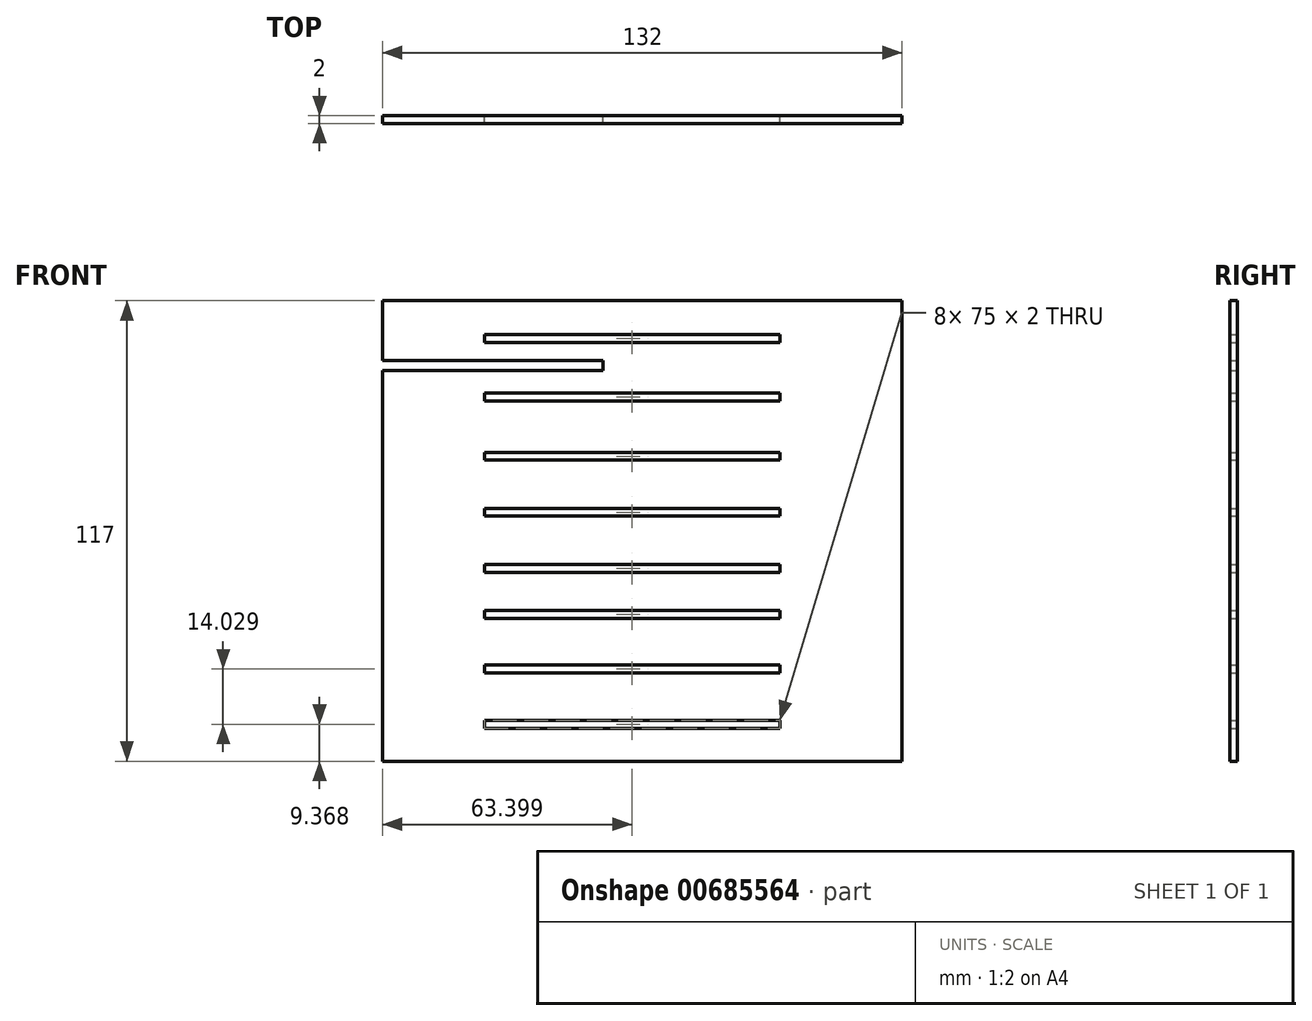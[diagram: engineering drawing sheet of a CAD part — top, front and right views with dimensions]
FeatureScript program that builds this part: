
annotation { "Feature Type Name" : "Feature", "Feature Type Description" : "" }
export const myFeature = defineFeature(function(context is Context, id is Id, definition is map)
    precondition{}
    {
        {
            var Q0;
            Q0=qCreatedBy(makeId("Front.planeOp"),FACE);
            var sketch = newSketch(context, id + "F0", { "sketchPlane" : qUnion([Q0])});
            skLineSegment(sketch, "E0.bottom", {"start": v(-36.75, -57.98) * mm, "end": v(38.25, -57.98) * mm});
            skLineSegment(sketch, "E0.top", {"start": v(-36.75, -59.98) * mm, "end": v(38.25, -59.98) * mm});
            skLineSegment(sketch, "E0.left", {"start": v(-36.75, -57.98) * mm, "end": v(-36.75, -59.98) * mm});
            skLineSegment(sketch, "E0.right", {"start": v(38.25, -57.98) * mm, "end": v(38.25, -59.98) * mm});
            skLineSegment(sketch, "E1.bottom", {"start": v(-53.7, -51.72) * mm, "end": v(-6.7, -51.72) * mm});
            skLineSegment(sketch, "E1.top", {"start": v(-53.7, -54.22) * mm, "end": v(-6.7, -54.22) * mm});
            skLineSegment(sketch, "E1.right", {"start": v(-6.7, -51.72) * mm, "end": v(-6.7, -54.22) * mm});
            skLineSegment(sketch, "E2.bottom", {"start": v(56.3, -51.72) * mm, "end": v(9.3, -51.72) * mm});
            skLineSegment(sketch, "E2.top", {"start": v(56.3, -54.22) * mm, "end": v(9.3, -54.22) * mm});
            skLineSegment(sketch, "E2.right", {"start": v(9.3, -51.72) * mm, "end": v(9.3, -54.22) * mm});
            skLineSegment(sketch, "E3.bottom", {"start": v(-36.75, -43.95) * mm, "end": v(38.25, -43.95) * mm});
            skLineSegment(sketch, "E3.top", {"start": v(-36.75, -45.95) * mm, "end": v(38.25, -45.95) * mm});
            skLineSegment(sketch, "E3.left", {"start": v(-36.75, -43.95) * mm, "end": v(-36.75, -45.95) * mm});
            skLineSegment(sketch, "E3.right", {"start": v(38.25, -43.95) * mm, "end": v(38.25, -45.95) * mm});
            skLineSegment(sketch, "E4.bottom", {"start": v(-53.7, -37.44) * mm, "end": v(-6.7, -37.44) * mm});
            skLineSegment(sketch, "E4.top", {"start": v(-53.7, -39.94) * mm, "end": v(-6.7, -39.94) * mm});
            skLineSegment(sketch, "E4.right", {"start": v(-6.7, -37.44) * mm, "end": v(-6.7, -39.94) * mm});
            skLineSegment(sketch, "E5.bottom", {"start": v(56.3, -37.44) * mm, "end": v(9.3, -37.44) * mm});
            skLineSegment(sketch, "E5.top", {"start": v(56.3, -39.94) * mm, "end": v(9.3, -39.94) * mm});
            skLineSegment(sketch, "E5.right", {"start": v(9.3, -37.44) * mm, "end": v(9.3, -39.94) * mm});
            skLineSegment(sketch, "E6.bottom", {"start": v(-36.75, -30.05) * mm, "end": v(38.25, -30.05) * mm});
            skLineSegment(sketch, "E6.top", {"start": v(-36.75, -32.05) * mm, "end": v(38.25, -32.05) * mm});
            skLineSegment(sketch, "E6.left", {"start": v(-36.75, -30.05) * mm, "end": v(-36.75, -32.05) * mm});
            skLineSegment(sketch, "E6.right", {"start": v(38.25, -30.05) * mm, "end": v(38.25, -32.05) * mm});
            skLineSegment(sketch, "E7.bottom", {"start": v(-53.7, -23.9) * mm, "end": v(-6.7, -23.9) * mm});
            skLineSegment(sketch, "E7.top", {"start": v(-53.7, -26.4) * mm, "end": v(-6.7, -26.4) * mm});
            skLineSegment(sketch, "E7.right", {"start": v(-6.7, -23.9) * mm, "end": v(-6.7, -26.4) * mm});
            skLineSegment(sketch, "E8.bottom", {"start": v(56.3, -23.9) * mm, "end": v(9.3, -23.9) * mm});
            skLineSegment(sketch, "E8.top", {"start": v(56.3, -26.4) * mm, "end": v(9.3, -26.4) * mm});
            skLineSegment(sketch, "E8.right", {"start": v(9.3, -23.9) * mm, "end": v(9.3, -26.4) * mm});
            skLineSegment(sketch, "E9.bottom", {"start": v(-36.75, -18.4) * mm, "end": v(38.25, -18.4) * mm});
            skLineSegment(sketch, "E9.top", {"start": v(-36.75, -20.4) * mm, "end": v(38.25, -20.4) * mm});
            skLineSegment(sketch, "E9.left", {"start": v(-36.75, -18.4) * mm, "end": v(-36.75, -20.4) * mm});
            skLineSegment(sketch, "E9.right", {"start": v(38.25, -18.4) * mm, "end": v(38.25, -20.4) * mm});
            skLineSegment(sketch, "E10.bottom", {"start": v(-53.7, -10.37) * mm, "end": v(-6.7, -10.37) * mm});
            skLineSegment(sketch, "E10.top", {"start": v(-53.7, -12.87) * mm, "end": v(-6.7, -12.87) * mm});
            skLineSegment(sketch, "E10.right", {"start": v(-6.7, -10.37) * mm, "end": v(-6.7, -12.87) * mm});
            skLineSegment(sketch, "E11.bottom", {"start": v(56.3, -10.37) * mm, "end": v(9.3, -10.37) * mm});
            skLineSegment(sketch, "E11.top", {"start": v(56.3, -12.87) * mm, "end": v(9.3, -12.87) * mm});
            skLineSegment(sketch, "E11.right", {"start": v(9.3, -10.37) * mm, "end": v(9.3, -12.87) * mm});
            skLineSegment(sketch, "E12.bottom", {"start": v(-36.75, -4.1) * mm, "end": v(38.25, -4.1) * mm});
            skLineSegment(sketch, "E12.top", {"start": v(-36.75, -6.1) * mm, "end": v(38.25, -6.1) * mm});
            skLineSegment(sketch, "E12.left", {"start": v(-36.75, -4.1) * mm, "end": v(-36.75, -6.1) * mm});
            skLineSegment(sketch, "E12.right", {"start": v(38.25, -4.1) * mm, "end": v(38.25, -6.1) * mm});
            skLineSegment(sketch, "E13.bottom", {"start": v(-53.7, 2.5) * mm, "end": v(-6.7, 2.5) * mm});
            skLineSegment(sketch, "E13.top", {"start": v(-53.7, 0) * mm, "end": v(-6.7, 0) * mm});
            skLineSegment(sketch, "E13.right", {"start": v(-6.7, 2.5) * mm, "end": v(-6.7, 0) * mm});
            skLineSegment(sketch, "E14.bottom", {"start": v(56.3, 2.5) * mm, "end": v(9.3, 2.5) * mm});
            skLineSegment(sketch, "E14.top", {"start": v(56.3, 0) * mm, "end": v(9.3, 0) * mm});
            skLineSegment(sketch, "E14.right", {"start": v(9.3, 2.5) * mm, "end": v(9.3, 0) * mm});
            skPoint(sketch, "E15.firstSnap0", {"position": v(-14.77, 8.13) * mm});
            skLineSegment(sketch, "E15.bottom", {"start": v(-36.75, 8.13) * mm, "end": v(38.25, 8.13) * mm});
            skLineSegment(sketch, "E15.top", {"start": v(-36.75, 10.13) * mm, "end": v(38.25, 10.13) * mm});
            skLineSegment(sketch, "E15.left", {"start": v(-36.75, 8.13) * mm, "end": v(-36.75, 10.13) * mm});
            skLineSegment(sketch, "E15.right", {"start": v(38.25, 8.13) * mm, "end": v(38.25, 10.13) * mm});
            skLineSegment(sketch, "E16.bottom", {"start": v(-53.7, 18) * mm, "end": v(-6.7, 18) * mm});
            skLineSegment(sketch, "E16.top", {"start": v(-53.7, 15.5) * mm, "end": v(-6.7, 15.5) * mm});
            skLineSegment(sketch, "E16.right", {"start": v(-6.7, 18) * mm, "end": v(-6.7, 15.5) * mm});
            skLineSegment(sketch, "E17.bottom", {"start": v(56.3, 18) * mm, "end": v(9.3, 18) * mm});
            skLineSegment(sketch, "E17.top", {"start": v(56.3, 15.5) * mm, "end": v(9.3, 15.5) * mm});
            skLineSegment(sketch, "E17.right", {"start": v(9.3, 18) * mm, "end": v(9.3, 15.5) * mm});
            skLineSegment(sketch, "E18.bottom", {"start": v(-36.75, 25.21) * mm, "end": v(38.25, 25.21) * mm});
            skLineSegment(sketch, "E18.top", {"start": v(-36.75, 23.21) * mm, "end": v(38.25, 23.21) * mm});
            skLineSegment(sketch, "E18.left", {"start": v(-36.75, 25.21) * mm, "end": v(-36.75, 23.21) * mm});
            skLineSegment(sketch, "E18.right", {"start": v(38.25, 25.21) * mm, "end": v(38.25, 23.21) * mm});
            skLineSegment(sketch, "E19.bottom", {"start": v(-53.7, 33.42) * mm, "end": v(-6.7, 33.42) * mm});
            skLineSegment(sketch, "E19.top", {"start": v(-53.7, 30.92) * mm, "end": v(-6.7, 30.92) * mm});
            skLineSegment(sketch, "E19.right", {"start": v(-6.7, 33.42) * mm, "end": v(-6.7, 30.92) * mm});
            skLineSegment(sketch, "E20.bottom", {"start": v(56.3, 33.42) * mm, "end": v(9.3, 33.42) * mm});
            skLineSegment(sketch, "E20.top", {"start": v(56.3, 30.92) * mm, "end": v(9.3, 30.92) * mm});
            skLineSegment(sketch, "E20.right", {"start": v(9.3, 33.42) * mm, "end": v(9.3, 30.92) * mm});
            skLineSegment(sketch, "E21.bottom", {"start": v(-36.75, 40.06) * mm, "end": v(38.25, 40.06) * mm});
            skLineSegment(sketch, "E21.top", {"start": v(-36.75, 38.06) * mm, "end": v(38.25, 38.06) * mm});
            skLineSegment(sketch, "E21.left", {"start": v(-36.75, 40.06) * mm, "end": v(-36.75, 38.06) * mm});
            skLineSegment(sketch, "E21.right", {"start": v(38.25, 40.06) * mm, "end": v(38.25, 38.06) * mm});
            skPoint(sketch, "E22.bottom.start.orphan", {"position": v(24.15, 53.7) * mm});
            skLineSegment(sketch, "E23", {"start": v(56.3, -62.69) * mm, "end": v(-53.7, -62.69) * mm});
            skLineSegment(sketch, "E24", {"start": v(-53.7, -62.69) * mm, "end": v(-53.7, -54.22) * mm});
            skLineSegment(sketch, "E25.trimOffspring", {"start": v(-53.7, 18) * mm, "end": v(-53.7, 30.92) * mm});
            skLineSegment(sketch, "E26.trimOffspring", {"start": v(-53.7, 33.42) * mm, "end": v(-53.7, 43.9) * mm});
            skLineSegment(sketch, "E27.trimOffspring", {"start": v(-53.7, -23.9) * mm, "end": v(-53.7, -12.87) * mm});
            skLineSegment(sketch, "E28.trimOffspring", {"start": v(-53.7, -37.44) * mm, "end": v(-53.7, -26.4) * mm});
            skLineSegment(sketch, "E29.trimOffspring", {"start": v(-53.7, -51.72) * mm, "end": v(-53.7, -39.94) * mm});
            skLineSegment(sketch, "E30", {"start": v(-53.7, 15.5) * mm, "end": v(-53.7, 2.5) * mm});
            skLineSegment(sketch, "E31", {"start": v(-53.7, 0) * mm, "end": v(-53.7, -10.37) * mm});
            skPoint(sketch, "E32.end.orphan", {"position": v(56.3, 38.06) * mm});
            skLineSegment(sketch, "E33", {"start": v(56.3, 30.92) * mm, "end": v(56.3, 18) * mm});
            skLineSegment(sketch, "E34", {"start": v(56.3, 15.5) * mm, "end": v(56.3, 2.5) * mm});
            skLineSegment(sketch, "E35", {"start": v(56.3, 0) * mm, "end": v(56.3, -10.37) * mm});
            skLineSegment(sketch, "E36", {"start": v(56.3, -12.87) * mm, "end": v(56.3, -23.9) * mm});
            skLineSegment(sketch, "E37", {"start": v(56.3, -26.4) * mm, "end": v(56.3, -37.44) * mm});
            skLineSegment(sketch, "E38", {"start": v(56.3, -39.94) * mm, "end": v(56.3, -51.72) * mm});
            skLineSegment(sketch, "E39", {"start": v(56.3, -55.54) * mm, "end": v(56.3, -62.69) * mm});
            skPoint(sketch, "E40.end.orphan", {"position": v(55.92, 33.42) * mm});
            skLineSegment(sketch, "E41", {"start": v(-53.7, 43.9) * mm, "end": v(53.85, 43.9) * mm});
            skLineSegment(sketch, "E42", {"start": v(56.3, 33.42) * mm, "end": v(56.3, 43.93) * mm});
            skLineSegment(sketch, "E43", {"start": v(56.3, 43.93) * mm, "end": v(53.85, 43.9) * mm});
            skLineSegment(sketch, "E44.bottom", {"start": v(-62.65, 48.65) * mm, "end": v(69.35, 48.65) * mm});
            skLineSegment(sketch, "E44.top", {"start": v(-62.65, -68.35) * mm, "end": v(69.35, -68.35) * mm});
            skLineSegment(sketch, "E44.left", {"start": v(-62.65, 48.65) * mm, "end": v(-62.65, 33.42) * mm});
            skLineSegment(sketch, "E44.right", {"start": v(69.35, 48.65) * mm, "end": v(69.35, -68.35) * mm});
            skLineSegment(sketch, "E45", {"start": v(-53.7, 33.42) * mm, "end": v(-62.65, 33.42) * mm});
            skLineSegment(sketch, "E46", {"start": v(-53.7, 30.92) * mm, "end": v(-62.65, 30.92) * mm});
            skLineSegment(sketch, "E47.trimOffspring", {"start": v(-62.65, 30.92) * mm, "end": v(-62.65, -68.35) * mm});
            skLineSegment(sketch, "E48", {"start": v(-53.7, 18) * mm, "end": v(-62.65, 18) * mm});
            skLineSegment(sketch, "E49", {"start": v(-62.65, 18) * mm, "end": v(-62.65, 15.5) * mm});
            skLineSegment(sketch, "E50", {"start": v(-62.65, 15.5) * mm, "end": v(-53.7, 15.5) * mm});
            skLineSegment(sketch, "E51", {"start": v(-53.7, 2.5) * mm, "end": v(-62.65, 2.5) * mm});
            skLineSegment(sketch, "E52", {"start": v(-62.65, 2.5) * mm, "end": v(-62.65, 0) * mm});
            skLineSegment(sketch, "E53", {"start": v(-62.65, 0) * mm, "end": v(-53.7, 0) * mm});
            skLineSegment(sketch, "E54", {"start": v(-53.7, -10.37) * mm, "end": v(-62.65, -10.37) * mm});
            skLineSegment(sketch, "E55", {"start": v(-62.65, -10.37) * mm, "end": v(-62.65, -12.87) * mm});
            skLineSegment(sketch, "E56", {"start": v(-62.65, -12.87) * mm, "end": v(-53.7, -12.87) * mm});
            skSolve(sketch);
        }
        {
            var Q0;
            Q0 = qSketchRegion(id + "F0", true);
            extrude(context, id + "F1", {"entities" : qUnion([Q0]), "depth" : 1 * mm, "offsetDistance" : 25 * mm});
        }
        {
            var Q0;
            Q0 = qSketchRegion(id + "F0", true);
            extrude(context, id + "F2", {"entities" : qUnion([Q0]), "operationType" : NewBodyOperationType.ADD, "depth" : 2 * mm, "offsetDistance" : 25 * mm});
        }
    });
